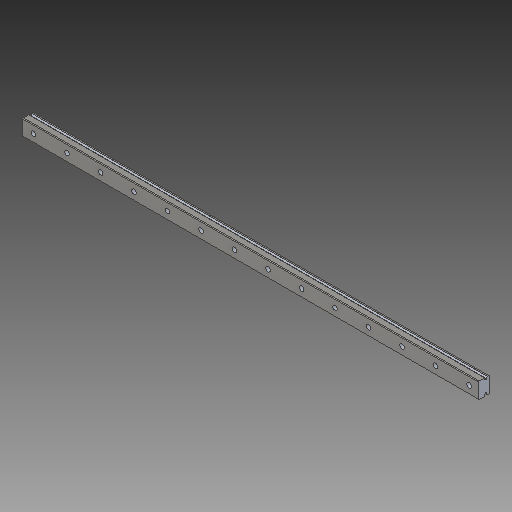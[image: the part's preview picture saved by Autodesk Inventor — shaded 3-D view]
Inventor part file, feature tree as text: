
AUTODESK INVENTOR PART (.ipt)
format: ipt  version: 2019 (Build 230136000, 136)  size: 187,904 bytes
history: native  units: mm
features: other x3, sketch x2
ambient origin geometry x8: Origin, YZ Plane, XZ Plane, XY Plane, X Axis, Y Axis, Z Axis, Center Point
bodies: Solid1 (feature_tree)
feature tree (5):
  other  "MGN12 Rail 300mm.ipt"
  other  "Solid1::MGN12 Rail 300mm.ipt"
  other  "TaggingFeature1"
  sketch  "Sketch1"  dims[d0=10.0mm]
  sketch  "Sketch3"
